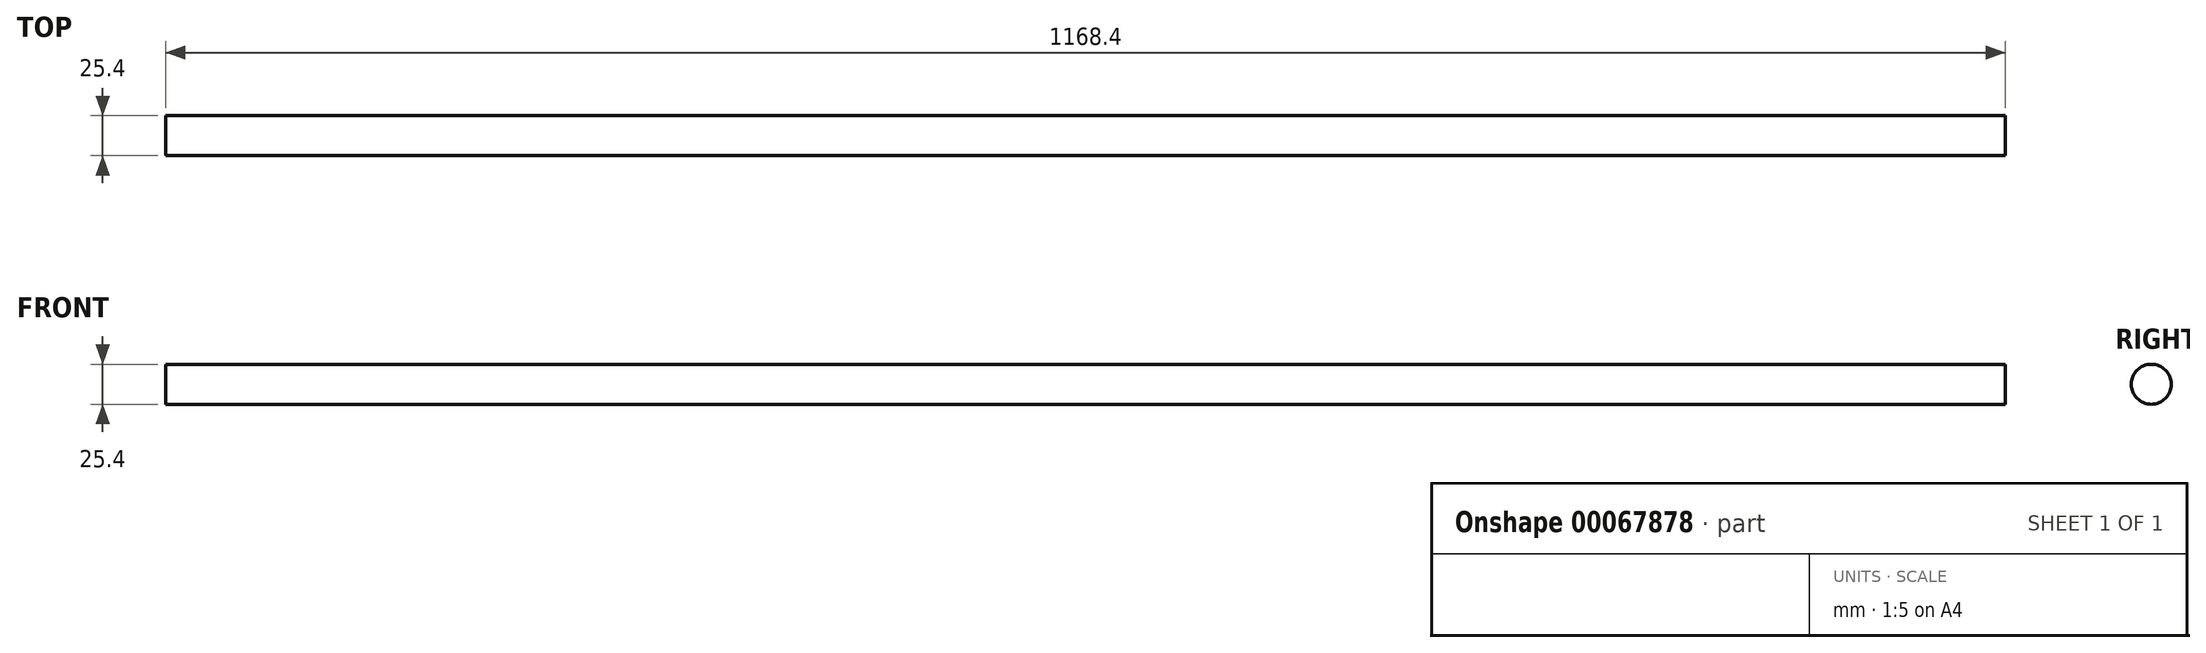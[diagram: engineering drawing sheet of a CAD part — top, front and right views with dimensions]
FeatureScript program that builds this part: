
annotation { "Feature Type Name" : "Feature", "Feature Type Description" : "" }
export const myFeature = defineFeature(function(context is Context, id is Id, definition is map)
    precondition{}
    {
        {
            var Q0;
            Q0=qCreatedBy(makeId("Right.planeOp"),FACE);
            var sketch = newSketch(context, id + "F0", { "sketchPlane" : qUnion([Q0])});
            skCircle(sketch, "E0", {"center": v(0, 0) * mm, "radius": 12.7 * mm});
            skSolve(sketch);
        }
        {
            var Q0;
            Q0=makeQuery(id+"F0.imprint","IMPRINT",FACE,{"disambiguationData":[TD([[makeQuery(id+"F0.imprint","IMPRINT",EDGE,{"derivedFrom":sQuery(id+"F0.wireOp",EDGE,"E0")}),1.0]])]});
            extrude(context, id + "F1", {"entities" : qUnion([Q0]), "depth" : 1168.4 * mm});
        }
    });
